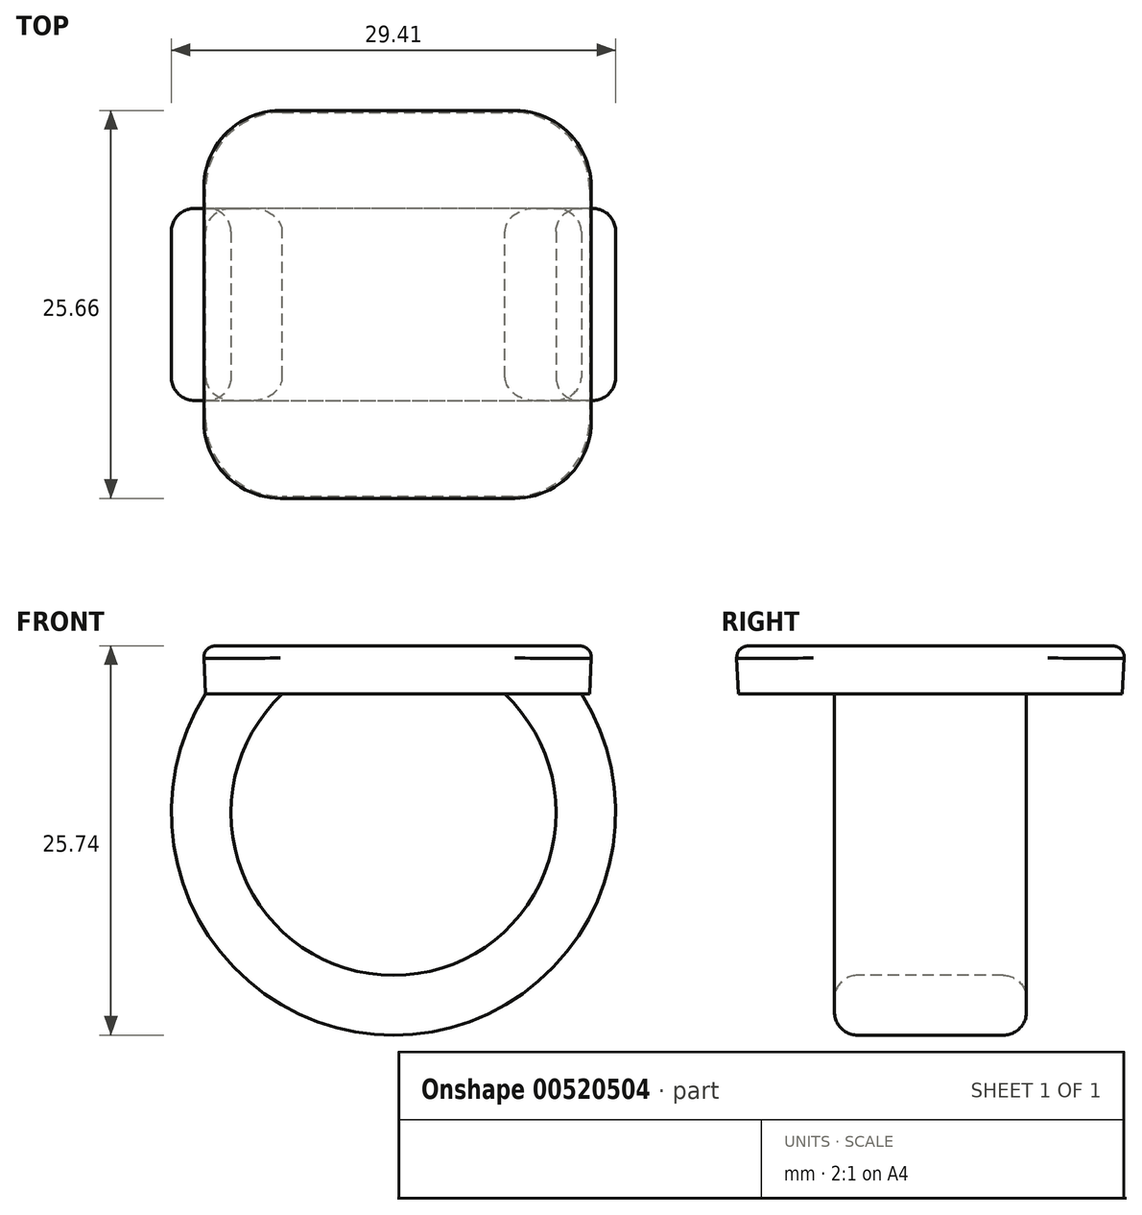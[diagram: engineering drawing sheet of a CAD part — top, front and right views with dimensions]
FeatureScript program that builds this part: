
annotation { "Feature Type Name" : "Feature", "Feature Type Description" : "" }
export const myFeature = defineFeature(function(context is Context, id is Id, definition is map)
    precondition{}
    {
        {
            var Q0;
            Q0=qCreatedBy(makeId("Top.planeOp"),FACE);
            var sketch = newSketch(context, id + "F0", { "sketchPlane" : qUnion([Q0])});
            skLineSegment(sketch, "E0.bottom", {"start": v(12.7, -12.7) * mm, "end": v(-12.7, -12.7) * mm});
            skLineSegment(sketch, "E0.top", {"start": v(12.7, 12.7) * mm, "end": v(-12.7, 12.7) * mm});
            skLineSegment(sketch, "E0.left", {"start": v(12.7, -12.7) * mm, "end": v(12.7, 12.7) * mm});
            skLineSegment(sketch, "E0.right", {"start": v(-12.7, -12.7) * mm, "end": v(-12.7, 12.7) * mm});
            skPoint(sketch, "E0.middle", {"position": v(0, 0) * mm});
            skSolve(sketch);
        }
        {
            var Q0;
            Q0=makeQuery(id+"F0.imprint","IMPRINT",FACE,{"disambiguationData":[TD([[makeQuery(id+"F0.imprint","IMPRINT",EDGE,{"derivedFrom":sQuery(id+"F0.wireOp",EDGE,"E0.bottom")}),-1.0]])]});
            extrude(context, id + "F1", {"entities" : qUnion([Q0]), "depth" : 3.17 * mm, "offsetDistance" : 25.4 * mm, "hasDraft" : true, "draftAngle" : 3 * degree});
        }
        {
            var Q0;
            Q0=qCreatedBy(makeId("Front.planeOp"),FACE);
            var sketch = newSketch(context, id + "F2", { "sketchPlane" : qUnion([Q0])});
            skArc(sketch, "E1", {"start": v(-11.78, 0) * mm, "mid": v(-0.27, -21.8) * mm, "end": v(11.25, 0) * mm});
            skSolve(sketch);
        }
        {
            var Q0;
            Q0=makeQuery(id+"F1.opExtrude","CAP_FACE",FACE,{"disambiguationData":[OSD([sQuery(id+"F0.wireOp",EDGE,"E0.bottom"),sQuery(id+"F0.wireOp",EDGE,"E0.top"),sQuery(id+"F0.wireOp",EDGE,"E0.left"),sQuery(id+"F0.wireOp",EDGE,"E0.right")])],"isStart":true});
            var sketch = newSketch(context, id + "F3", { "sketchPlane" : qUnion([Q0])});
            skLineSegment(sketch, "E2.bottom", {"start": v(-12.7, 6.35) * mm, "end": v(-7.62, 6.35) * mm});
            skLineSegment(sketch, "E2.top", {"start": v(-12.7, -6.35) * mm, "end": v(-7.62, -6.35) * mm});
            skLineSegment(sketch, "E2.left", {"start": v(-12.7, 6.35) * mm, "end": v(-12.7, -6.35) * mm});
            skLineSegment(sketch, "E2.right", {"start": v(-7.62, 6.35) * mm, "end": v(-7.62, -6.35) * mm});
            skPoint(sketch, "E2.middle", {"position": v(-10.16, 0) * mm});
            skSolve(sketch);
        }
        {
            var Q0;
            Q0 = qSketchRegion(id + "F3", true);
            var Q1;
            Q1 = qConstructionFilter(qBodyType(qCreatedBy(id + "F2" ,EDGE), BodyType.WIRE), ConstructionObject.NO);
            sweep(context, id + "F4", {"operationType" : NewBodyOperationType.ADD, "profiles" : qUnion([Q0]), "path" : qUnion([Q1])});
        }
        {
            var Q0;
            Q0=qCreatedBy(makeId("Front.planeOp"),FACE);
            var sketch = newSketch(context, id + "F5", { "sketchPlane" : qUnion([Q0])});
            skPoint(sketch, "E3.0.end.orphan", {"position": v(11.25, 0) * mm});
            skPoint(sketch, "E3.0.start.orphan", {"position": v(9.73, -3.87) * mm});
            skLineSegment(sketch, "E4.0", {"start": v(9.73, -3.87) * mm, "end": v(11.25, 0) * mm});
            skLineSegment(sketch, "E4.1", {"start": v(12.7, 0) * mm, "end": v(7.08, 0) * mm});
            skArc(sketch, "E4.2", {"start": v(9.73, -3.87) * mm, "mid": v(8.62, -1.8) * mm, "end": v(7.08, 0) * mm});
            skPoint(sketch, "E5.orphan", {"position": v(-7.62, 0) * mm});
            skLineSegment(sketch, "E6.trimOffspring", {"start": v(-7.62, 0) * mm, "end": v(-12.7, 0) * mm});
            skSolve(sketch);
        }
        {
            var Q0;
            Q0 = qSketchRegion(id + "F5", true);
            var Q1;
            Q1=makeQuery(id+"F4.opSweep","SWEPT_FACE",FACE,{"disambiguationData":[OSD([sQuery(id+"F2.wireOp",EDGE,"E1"),sQuery(id+"F3.wireOp",EDGE,"E2.bottom")])]});
            var Q2;
            Q2=makeQuery(id+"F4.opSweep","SWEPT_FACE",FACE,{"disambiguationData":[OSD([sQuery(id+"F2.wireOp",EDGE,"E1"),sQuery(id+"F3.wireOp",EDGE,"E2.top")])]});
            extrude(context, id + "F6", {"entities" : qUnion([Q0]), "operationType" : NewBodyOperationType.ADD, "endBound" : BoundingType.UP_TO_SURFACE, "depth" : 25.4 * mm, "endBoundEntityFace" : qUnion([Q1]), "offsetDistance" : 25.4 * mm, "hasSecondDirection" : true, "secondDirectionBound" : SecondDirectionBoundingType.UP_TO_SURFACE, "secondDirectionOppositeDirection" : true, "secondDirectionDepth" : 25.4 * mm, "secondDirectionBoundEntityFace" : qUnion([Q2])});
        }
        {
            var Q0;
            Q0=makeQuery(id+"F1.opExtrude","SWEPT_EDGE",EDGE,{"disambiguationData":[OSD([sQuery(id+"F0.wireOp",EDGE,"E0.bottom"),sQuery(id+"F0.wireOp",EDGE,"E0.left")])]});
            var Q1;
            Q1=makeQuery(id+"F1.opExtrude","SWEPT_EDGE",EDGE,{"disambiguationData":[OSD([sQuery(id+"F0.wireOp",EDGE,"E0.bottom"),sQuery(id+"F0.wireOp",EDGE,"E0.right")])]});
            var Q2;
            Q2=makeQuery(id+"F1.opExtrude","SWEPT_EDGE",EDGE,{"disambiguationData":[OSD([sQuery(id+"F0.wireOp",EDGE,"E0.top"),sQuery(id+"F0.wireOp",EDGE,"E0.right")])]});
            var Q3;
            Q3=makeQuery(id+"F1.opExtrude","SWEPT_EDGE",EDGE,{"disambiguationData":[OSD([sQuery(id+"F0.wireOp",EDGE,"E0.top"),sQuery(id+"F0.wireOp",EDGE,"E0.left")])]});
            fillet(context, id + "F7", {"entities" : qUnion([Q0, Q1, Q2, Q3]), "radius" : 5.08 * mm, "tangentPropagation" : true, "allowEdgeOverflow" : false});
        }
        {
            var Q0;
            {var subQ0=sQuery(id+"F3.wireOp",EDGE,"E2.bottom");var subQ1=sQuery(id+"F2.wireOp",EDGE,"E1");Q0=makeQuery(id+"F6.boolean.opBoolean","MERGE",EDGE,{"derivedFrom":[makeQuery(id+"F4.opSweep","SWEPT_EDGE",EDGE,{"disambiguationData":[OSD([subQ1,subQ0,sQuery(id+"F3.wireOp",EDGE,"E2.right")])]}),makeQuery(id+"F6.opExtrude","TWEAK_EDGE",EDGE,{"derivedFrom":[makeQuery(id+"F4.opSweep","SWEPT_FACE",FACE,{"disambiguationData":[OSD([subQ1,subQ0])]}),makeQuery(id+"F5.imprint","IMPRINT",EDGE,{"derivedFrom":sQuery(id+"F5.wireOp",EDGE,"E4.2")})]})]});}
            var Q1;
            Q1=makeQuery(id+"F4.opSweep","SWEPT_EDGE",EDGE,{"disambiguationData":[OSD([sQuery(id+"F0.wireOp",EDGE,"E0.right"),sQuery(id+"F2.wireOp",EDGE,"E1"),sQuery(id+"F3.wireOp",EDGE,"E2.bottom"),sQuery(id+"F3.wireOp",EDGE,"E2.left")])]});
            var Q2;
            {var subQ0=sQuery(id+"F3.wireOp",EDGE,"E2.top");var subQ1=sQuery(id+"F2.wireOp",EDGE,"E1");Q2=makeQuery(id+"F6.boolean.opBoolean","MERGE",EDGE,{"derivedFrom":[makeQuery(id+"F4.opSweep","SWEPT_EDGE",EDGE,{"disambiguationData":[OSD([subQ1,subQ0,sQuery(id+"F3.wireOp",EDGE,"E2.right")])]}),makeQuery(id+"F6.opExtrude","TWEAK_EDGE",EDGE,{"derivedFrom":[makeQuery(id+"F4.opSweep","SWEPT_FACE",FACE,{"disambiguationData":[OSD([subQ1,subQ0])]}),makeQuery(id+"F5.imprint","IMPRINT",EDGE,{"derivedFrom":sQuery(id+"F5.wireOp",EDGE,"E4.2")})]})]});}
            var Q3;
            Q3=makeQuery(id+"F4.opSweep","SWEPT_EDGE",EDGE,{"disambiguationData":[OSD([sQuery(id+"F0.wireOp",EDGE,"E0.right"),sQuery(id+"F2.wireOp",EDGE,"E1"),sQuery(id+"F3.wireOp",EDGE,"E2.top"),sQuery(id+"F3.wireOp",EDGE,"E2.left")])]});
            fillet(context, id + "F8", {"entities" : qUnion([Q0, Q1, Q2, Q3]), "radius" : 1.52 * mm, "tangentPropagation" : true, "allowEdgeOverflow" : false});
        }
        {
            var Q0;
            Q0=makeQuery(id+"F1.opExtrude","CAP_FACE",FACE,{"disambiguationData":[OSD([sQuery(id+"F0.wireOp",EDGE,"E0.bottom"),sQuery(id+"F0.wireOp",EDGE,"E0.top"),sQuery(id+"F0.wireOp",EDGE,"E0.left"),sQuery(id+"F0.wireOp",EDGE,"E0.right")])],"isStart":false});
            fillet(context, id + "F9", {"entities" : qUnion([Q0]), "radius" : 0.76 * mm, "tangentPropagation" : true, "allowEdgeOverflow" : false});
        }
    });
